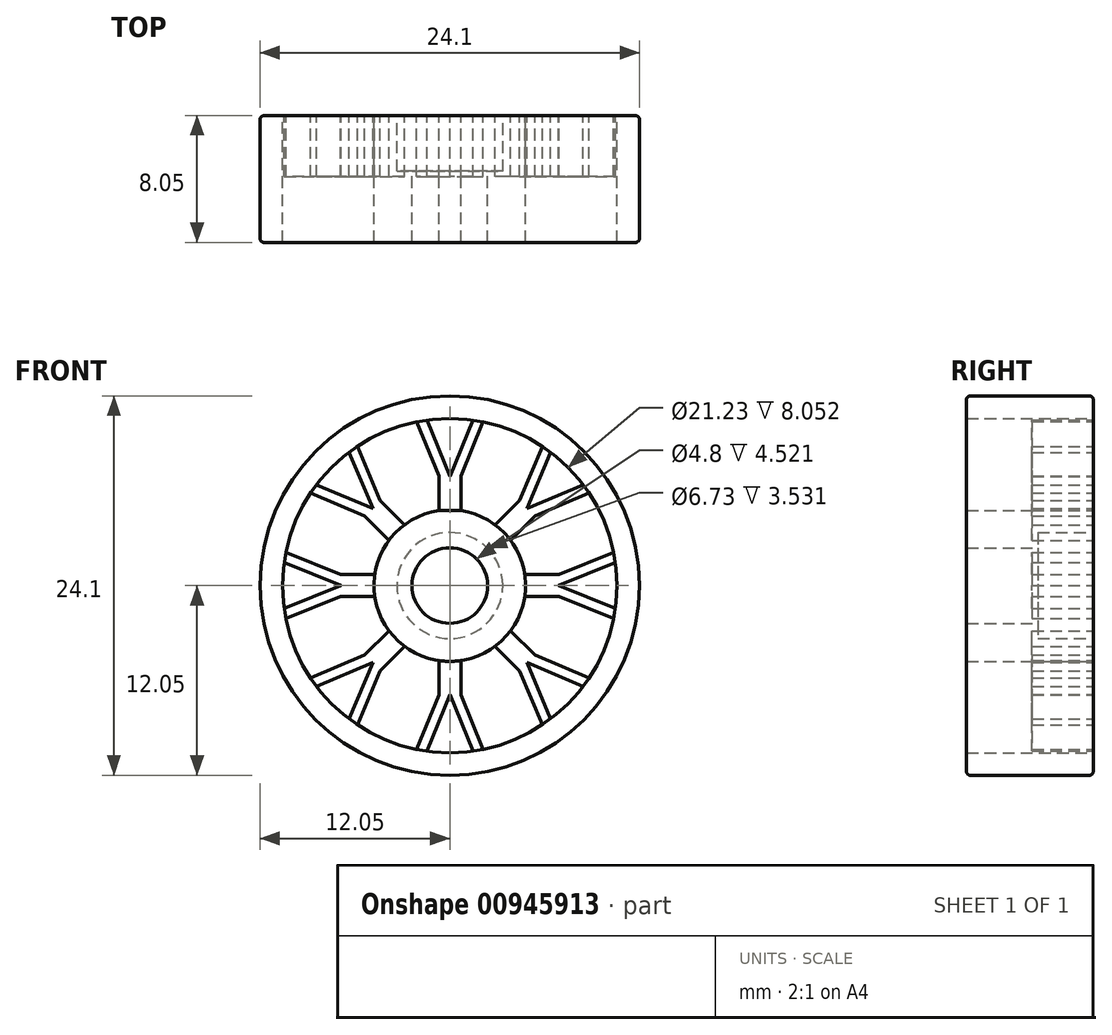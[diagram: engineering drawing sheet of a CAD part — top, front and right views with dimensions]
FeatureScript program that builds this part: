
annotation { "Feature Type Name" : "Feature", "Feature Type Description" : "" }
export const myFeature = defineFeature(function(context is Context, id is Id, definition is map)
    precondition{}
    {
        {
            var Q0;
            Q0=qCreatedBy(makeId("Front.planeOp"),FACE);
            var sketch = newSketch(context, id + "F0", { "sketchPlane" : qUnion([Q0])});
            skCircle(sketch, "E0", {"center": v(0, 0) * mm, "radius": 12.05 * mm});
            skCircle(sketch, "E1", {"center": v(0, 0) * mm, "radius": 10.62 * mm});
            skCircle(sketch, "E2", {"center": v(0, 0) * mm, "radius": 4.81 * mm});
            skLineSegment(sketch, "E3.bottom", {"start": v(-0.7, 6.95) * mm, "end": v(0.7, 6.95) * mm});
            skLineSegment(sketch, "E3.top", {"start": v(-0.7, 4.76) * mm, "end": v(0.7, 4.76) * mm});
            skLineSegment(sketch, "E3.left", {"start": v(-0.7, 6.95) * mm, "end": v(-0.7, 4.76) * mm});
            skLineSegment(sketch, "E3.right", {"start": v(0.7, 6.95) * mm, "end": v(0.7, 4.76) * mm});
            skLineSegment(sketch, "E4", {"start": v(-0.7, 6.95) * mm, "end": v(-2.1, 10.4) * mm});
            skLineSegment(sketch, "E5", {"start": v(0.7, 6.95) * mm, "end": v(2.1, 10.4) * mm});
            skLineSegment(sketch, "E6", {"start": v(-1.46, 10.52) * mm, "end": v(0, 6.91) * mm});
            skLineSegment(sketch, "E7", {"start": v(1.46, 10.52) * mm, "end": v(0, 6.91) * mm});
            skSolve(sketch);
        }
        {
            var Q0;
            {var subQ0=sQuery(id+"F0.wireOp",EDGE,"E3.left");Q0=makeQuery(id+"F0.imprint","IMPRINT",FACE,{"disambiguationData":[TD([[makeQuery(id+"F0.imprint","IMPRINT",EDGE,{"derivedFrom":subQ0}),1.0]])]});}
            var Q1;
            {var subQ0=sQuery(id+"F0.wireOp",EDGE,"E5");Q1=makeQuery(id+"F0.imprint","IMPRINT",FACE,{"disambiguationData":[TD([[makeQuery(id+"F0.imprint","IMPRINT",EDGE,{"derivedFrom":subQ0}),1.0]])]});}
            var Q2;
            {var subQ0=sQuery(id+"F0.wireOp",EDGE,"E4");Q2=makeQuery(id+"F0.imprint","IMPRINT",FACE,{"disambiguationData":[TD([[makeQuery(id+"F0.imprint","IMPRINT",EDGE,{"derivedFrom":subQ0}),-1.0]])]});}
            extrude(context, id + "F1", {"entities" : qUnion([Q0, Q1, Q2]), "depth" : 3.9 * mm, "offsetDistance" : 25.4 * mm});
        }
        {
            var Q0;
            Q0=makeQuery(id+"F1.opExtrude","SWEPT_BODY",BODY,{"disambiguationData":[OSD([sQuery(id+"F0.wireOp",EDGE,"E1"),sQuery(id+"F0.wireOp",EDGE,"E2"),sQuery(id+"F0.wireOp",EDGE,"E3.left"),sQuery(id+"F0.wireOp",EDGE,"E3.right"),sQuery(id+"F0.wireOp",EDGE,"E4"),sQuery(id+"F0.wireOp",EDGE,"E5"),sQuery(id+"F0.wireOp",EDGE,"E6"),sQuery(id+"F0.wireOp",EDGE,"E7")])]});
            var Q1;
            Q1=sQuery(id+"F0.wireOp",EDGE,"E2");
            circularPattern(context, id + "F2", {"entities" : qUnion([Q0]), "axis" : qUnion([Q1]), "angle" : 360 * degree, "instanceCount" : 8, "equalSpace" : true});
        }
        {
            var Q0;
            Q0=makeQuery(id+"F0.imprint","IMPRINT",FACE,{"disambiguationData":[TD([[makeQuery(id+"F0.imprint","IMPRINT",EDGE,{"derivedFrom":sQuery(id+"F0.wireOp",EDGE,"E0")}),1.0]])]});
            var Q1;
            {var subQ0=sQuery(id+"F0.wireOp",EDGE,"E3.top");Q1=makeQuery(id+"F0.imprint","IMPRINT",FACE,{"disambiguationData":[TD([[makeQuery(id+"F0.imprint","IMPRINT",EDGE,{"derivedFrom":subQ0}),-1.0]])]});}
            extrude(context, id + "F3", {"entities" : qUnion([Q0, Q1]), "depth" : 8.05 * mm, "offsetDistance" : 25.4 * mm});
        }
        {
            var Q0;
            Q0=sQuery(id+"F0.wireOp",VERTEX,"E0.center");
            var Q1;
            Q1=makeQuery(id+"F3.opExtrude","SWEPT_BODY",BODY,{"disambiguationData":[OSD([sQuery(id+"F0.wireOp",EDGE,"E2"),sQuery(id+"F0.wireOp",EDGE,"E3.top")])]});
            hole(context, id + "F4", {"style" : HoleStyle.C_BORE, "endStyle" : HoleEndStyle.THROUGH, "oppositeDirection" : true, "holeDiameter" : 4.8 * mm, "cBoreDiameter" : 6.73 * mm, "cBoreDepth" : 3.53 * mm, "majorDiameter" : 6.35 * mm, "isTappedThrough" : true, "tappedDepth" : 12.7 * mm, "tapClearance" : 3, "locations" : qUnion([Q0]), "scope" : qUnion([Q1])});
        }
        {
            var Q0;
            Q0=makeQuery(id+"F3.opExtrude","CAP_EDGE",EDGE,{"disambiguationData":[OSD([sQuery(id+"F0.wireOp",EDGE,"E0")])],"isStart":false});
            var Q1;
            Q1=makeQuery(id+"F3.opExtrude","CAP_EDGE",EDGE,{"disambiguationData":[OSD([sQuery(id+"F0.wireOp",EDGE,"E0")])],"isStart":true});
            fillet(context, id + "F5", {"entities" : qUnion([Q0, Q1]), "radius" : 0.25 * mm, "tangentPropagation" : true, "allowEdgeOverflow" : false});
        }
        {
            var Q0;
            {var subQ0=sQuery(id+"F0.wireOp",EDGE,"E3.top");Q0=makeQuery(id+"F0.imprint","IMPRINT",FACE,{"disambiguationData":[TD([[makeQuery(id+"F0.imprint","IMPRINT",EDGE,{"derivedFrom":subQ0}),1.0]])]});}
            var Q1;
            Q1=makeQuery(id+"F1.opExtrude","CAP_FACE",FACE,{"disambiguationData":[OSD([sQuery(id+"F0.wireOp",EDGE,"E1"),sQuery(id+"F0.wireOp",EDGE,"E2"),sQuery(id+"F0.wireOp",EDGE,"E3.left"),sQuery(id+"F0.wireOp",EDGE,"E3.right"),sQuery(id+"F0.wireOp",EDGE,"E4"),sQuery(id+"F0.wireOp",EDGE,"E5"),sQuery(id+"F0.wireOp",EDGE,"E6"),sQuery(id+"F0.wireOp",EDGE,"E7")])],"isStart":false});
            extrude(context, id + "F6", {"entities" : qUnion([Q0]), "operationType" : NewBodyOperationType.ADD, "endBound" : BoundingType.UP_TO_SURFACE, "depth" : 25.4 * mm, "endBoundEntityFace" : qUnion([Q1]), "offsetDistance" : 25.4 * mm});
        }
    });
